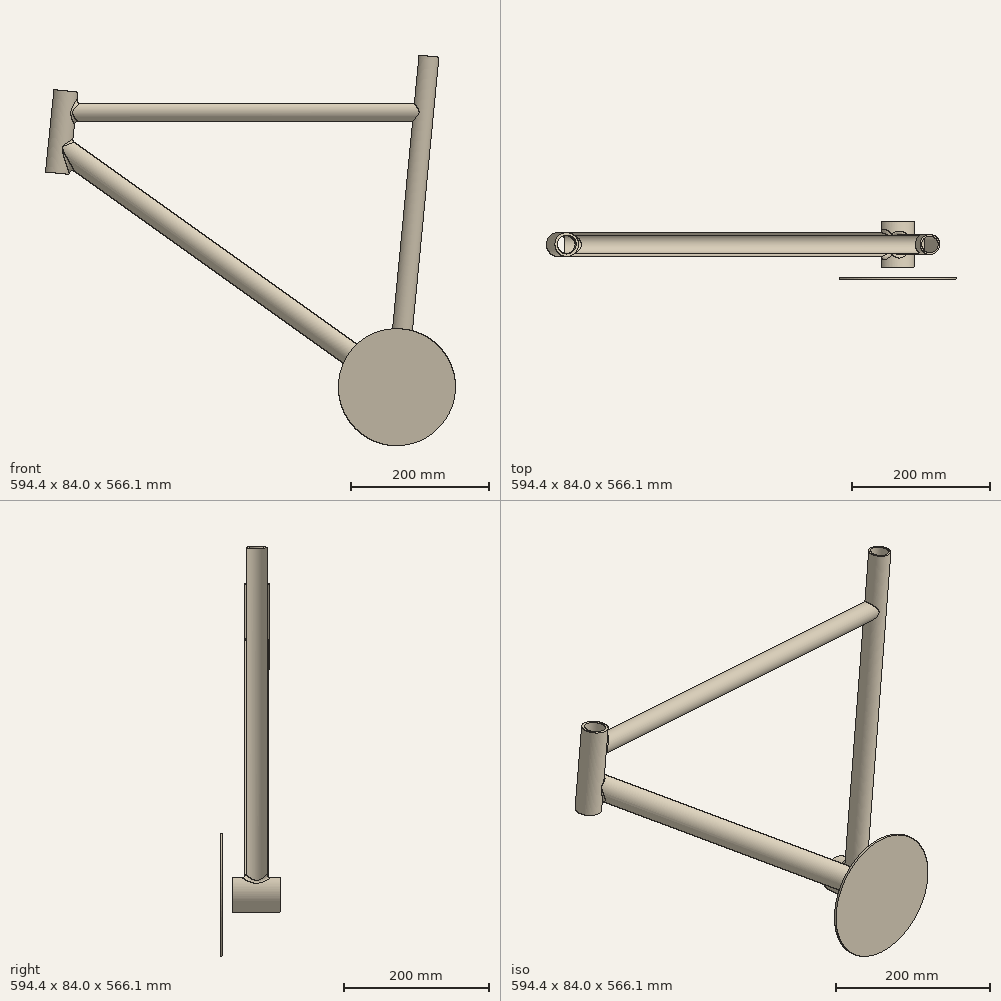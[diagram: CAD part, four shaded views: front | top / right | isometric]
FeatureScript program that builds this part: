
annotation { "Feature Type Name" : "Feature", "Feature Type Description" : "" }
export const myFeature = defineFeature(function(context is Context, id is Id, definition is map)
    precondition{}
    {
        {
            var Q0;
            Q0=qCreatedBy(makeId("Front.planeOp"),FACE);
            var sketch = newSketch(context, id + "F0", { "sketchPlane" : qUnion([Q0])});
            skLineSegment(sketch, "E0", {"start": v(0, 0) * mm, "end": v(-488.26, 348.72) * mm});
            skLineSegment(sketch, "E1", {"start": v(0, 0) * mm, "end": v(46.5, 479.84) * mm});
            skLineSegment(sketch, "E2", {"start": v(-483.17, 398.14) * mm, "end": v(38.58, 398.14) * mm});
            skCircle(sketch, "E3", {"center": v(0, 0) * mm, "radius": 24.13 * mm});
            skLineSegment(sketch, "E4", {"start": v(38.58, 398.14) * mm, "end": v(398.64, 35.69) * mm});
            skLineSegment(sketch, "E5", {"start": v(398.64, 35.69) * mm, "end": v(0, 0) * mm});
            skCircle(sketch, "E6", {"center": v(398.64, 35.69) * mm, "radius": 330.2 * mm, "construction": true});
            skLineSegment(sketch, "E7", {"start": v(-483.17, 398.14) * mm, "end": v(-488.26, 348.72) * mm});
            skLineSegment(sketch, "E8", {"start": v(-483.17, 398.14) * mm, "end": v(-483.17, 489.5) * mm, "construction": true});
            skSolve(sketch);
        }
        {
            var Q0;
            {var subQ1=sQuery(id+"F0.wireOp",EDGE,"E0");var subQ3=sQuery(id+"F0.wireOp",EDGE,"E3");var subQ4=makeQuery(id+"F0.imprint","INTERSECT",VERTEX,{"derivedFrom":[subQ1,subQ3]});Q0=makeQuery(id+"F0.imprint","IMPRINT",FACE,{"disambiguationData":[TD([[makeQuery(id+"F0.imprint","IMPRINT",EDGE,{"disambiguationData":[TD([[subQ4,1.0]])],"derivedFrom":subQ3}),1.0]])]});}
            var Q1;
            {var subQ0=sQuery(id+"F0.wireOp",EDGE,"E5");var subQ3=sQuery(id+"F0.wireOp",EDGE,"E3");var subQ5=makeQuery(id+"F0.imprint","INTERSECT",VERTEX,{"derivedFrom":[subQ3,subQ0]});Q1=makeQuery(id+"F0.imprint","IMPRINT",FACE,{"disambiguationData":[TD([[makeQuery(id+"F0.imprint","IMPRINT",EDGE,{"disambiguationData":[TD([[subQ5,-1.0]])],"derivedFrom":subQ3}),1.0]])]});}
            var Q2;
            {var subQ1=sQuery(id+"F0.wireOp",EDGE,"E0");var subQ3=sQuery(id+"F0.wireOp",EDGE,"E3");var subQ4=makeQuery(id+"F0.imprint","INTERSECT",VERTEX,{"derivedFrom":[subQ1,subQ3]});Q2=makeQuery(id+"F0.imprint","IMPRINT",FACE,{"disambiguationData":[TD([[makeQuery(id+"F0.imprint","IMPRINT",EDGE,{"disambiguationData":[TD([[subQ4,-1.0]])],"derivedFrom":subQ3}),1.0]])]});}
            var Q3;
            Q3=sQuery(id+"F0.wireOp",EDGE,"E3");
            extrude(context, id + "F1", {"entities" : qUnion([Q0, Q1, Q2]), "surfaceEntities" : qUnion([Q3]), "endBound" : BoundingType.SYMMETRIC, "depth" : 67 * mm, "offsetDistance" : 25 * mm});
        }
        {
            var Q0;
            Q0=qCreatedBy(makeId("Front.planeOp"),FACE);
            var sketch = newSketch(context, id + "F2", { "sketchPlane" : qUnion([Q0])});
            skLineSegment(sketch, "E9.0", {"start": v(0, 0) * mm, "end": v(46.5, 479.84) * mm, "construction": true});
            skCircle(sketch, "E10.0", {"center": v(0, 0) * mm, "radius": 24.13 * mm});
            skLineSegment(sketch, "E11", {"start": v(0, 0) * mm, "end": v(-14.43, 1.4) * mm});
            skLineSegment(sketch, "E12", {"start": v(-14.43, 1.4) * mm, "end": v(32.06, 481.24) * mm});
            skLineSegment(sketch, "E13", {"start": v(32.06, 481.24) * mm, "end": v(46.5, 479.84) * mm});
            skLineSegment(sketch, "E14", {"start": v(34.54, 481) * mm, "end": v(-11.95, 1.16) * mm});
            skSolve(sketch);
        }
        {
            var Q0;
            {var subQ0=sQuery(id+"F2.wireOp",EDGE,"E13");Q0=makeQuery(id+"F2.imprint","IMPRINT",FACE,{"disambiguationData":[TD([[makeQuery(id+"F2.imprint","IMPRINT",EDGE,{"derivedFrom":subQ0}),-1.0]])]});}
            var Q1;
            Q1=sQuery(id+"F2.wireOp",EDGE,"E9.0");
            revolve(context, id + "F3", {"surfaceOperationType" : NewSurfaceOperationType.NEW, "entities" : qUnion([Q0]), "axis" : qUnion([Q1]), "revolveType" : RevolveType.FULL});
        }
        {
            var Q0;
            Q0=qCreatedBy(makeId("Front.planeOp"),FACE);
            var sketch = newSketch(context, id + "F4", { "sketchPlane" : qUnion([Q0])});
            skLineSegment(sketch, "E15", {"start": v(-479.93, 429.59) * mm, "end": v(-462.64, 427.8) * mm});
            skLineSegment(sketch, "E16", {"start": v(-462.64, 427.8) * mm, "end": v(-474.94, 308.44) * mm});
            skLineSegment(sketch, "E17", {"start": v(-474.94, 308.44) * mm, "end": v(-492.23, 310.22) * mm});
            skLineSegment(sketch, "E18", {"start": v(-466.36, 428.19) * mm, "end": v(-478.66, 308.82) * mm});
            skLineSegment(sketch, "E19.0", {"start": v(-479.93, 429.59) * mm, "end": v(-492.23, 310.22) * mm, "construction": true});
            skPoint(sketch, "E20.orphan", {"position": v(-483.17, 398.14) * mm});
            skPoint(sketch, "E21.orphan", {"position": v(-488.26, 348.72) * mm});
            skSolve(sketch);
        }
        {
            var Q0;
            Q0 = qSketchRegion(id + "F4", true);
            var Q1;
            Q1=sQuery(id+"F0.wireOp",EDGE,"E7");
            revolve(context, id + "F5", {"surfaceOperationType" : NewSurfaceOperationType.NEW, "entities" : qUnion([Q0]), "axis" : qUnion([Q1]), "revolveType" : RevolveType.FULL});
        }
        {
            var Q0;
            Q0=qCreatedBy(makeId("Front.planeOp"),FACE);
            var sketch = newSketch(context, id + "F6", { "sketchPlane" : qUnion([Q0])});
            skLineSegment(sketch, "E22.0", {"start": v(-483.17, 398.14) * mm, "end": v(38.58, 398.14) * mm, "construction": true});
            skLineSegment(sketch, "E23", {"start": v(-483.17, 398.14) * mm, "end": v(-483.17, 385.14) * mm});
            skLineSegment(sketch, "E24", {"start": v(-483.17, 385.14) * mm, "end": v(38.58, 385.14) * mm});
            skLineSegment(sketch, "E25", {"start": v(38.58, 385.14) * mm, "end": v(38.58, 398.14) * mm});
            skLineSegment(sketch, "E26", {"start": v(-483.17, 386.14) * mm, "end": v(38.58, 386.14) * mm});
            skSolve(sketch);
        }
        {
            var Q0;
            Q0 = qSketchRegion(id + "F6", true);
            var Q1;
            Q1=sQuery(id+"F0.wireOp",EDGE,"E2");
            revolve(context, id + "F7", {"surfaceOperationType" : NewSurfaceOperationType.NEW, "entities" : qUnion([Q0]), "axis" : qUnion([Q1]), "revolveType" : RevolveType.FULL});
        }
        {
            var Q0;
            Q0=qCreatedBy(makeId("Front.planeOp"),FACE);
            var sketch = newSketch(context, id + "F8", { "sketchPlane" : qUnion([Q0])});
            skLineSegment(sketch, "E27.0", {"start": v(0, 0) * mm, "end": v(-488.26, 348.72) * mm, "construction": true});
            skLineSegment(sketch, "E28", {"start": v(-488.26, 348.72) * mm, "end": v(-498.14, 334.88) * mm});
            skLineSegment(sketch, "E29", {"start": v(-498.14, 334.88) * mm, "end": v(-9.88, -13.83) * mm});
            skLineSegment(sketch, "E30", {"start": v(-9.88, -13.83) * mm, "end": v(0, 0) * mm});
            skLineSegment(sketch, "E31", {"start": v(-497.56, 335.7) * mm, "end": v(-9.3, -13.02) * mm});
            skSolve(sketch);
        }
        {
            var Q0;
            Q0 = qSketchRegion(id + "F8", true);
            var Q1;
            Q1=sQuery(id+"F8.wireOp",EDGE,"E27.0");
            revolve(context, id + "F9", {"surfaceOperationType" : NewSurfaceOperationType.NEW, "entities" : qUnion([Q0]), "axis" : qUnion([Q1]), "revolveType" : RevolveType.FULL});
        }
        {
            var Q0;
            Q0=makeQuery(id+"F5.opRevolve","SWEPT_BODY",BODY,{"disambiguationData":[OSD([sQuery(id+"F4.wireOp",EDGE,"E15"),sQuery(id+"F4.wireOp",EDGE,"E16"),sQuery(id+"F4.wireOp",EDGE,"E17"),sQuery(id+"F4.wireOp",EDGE,"E18")])]});
            var Q1;
            Q1=makeQuery(id+"F3.opRevolve","SWEPT_BODY",BODY,{"disambiguationData":[OSD([sQuery(id+"F2.wireOp",EDGE,"E10.0"),sQuery(id+"F2.wireOp",EDGE,"E12"),sQuery(id+"F2.wireOp",EDGE,"E13"),sQuery(id+"F2.wireOp",EDGE,"E14")])]});
            var Q2;
            Q2=makeQuery(id+"F7.opRevolve","SWEPT_BODY",BODY,{"disambiguationData":[OSD([sQuery(id+"F6.wireOp",EDGE,"E23"),sQuery(id+"F6.wireOp",EDGE,"E24"),sQuery(id+"F6.wireOp",EDGE,"E25"),sQuery(id+"F6.wireOp",EDGE,"E26")])]});
            var Q3;
            Q3=makeQuery(id+"F9.opRevolve","SWEPT_BODY",BODY,{"disambiguationData":[OSD([sQuery(id+"F8.wireOp",EDGE,"E28"),sQuery(id+"F8.wireOp",EDGE,"E29"),sQuery(id+"F8.wireOp",EDGE,"E30"),sQuery(id+"F8.wireOp",EDGE,"E31")])]});
            booleanBodies(context, id + "F10", {"operationType" : BooleanOperationType.SUBTRACTION, "tools" : qUnion([Q0, Q1]), "targets" : qUnion([Q2, Q3]), "keepTools" : true});
        }
        {
            var Q0;
            Q0=makeQuery(id+"F1.opExtrude","SWEPT_BODY",BODY,{"disambiguationData":[OSD([sQuery(id+"F0.wireOp",EDGE,"E3")])]});
            var Q1;
            Q1=makeQuery(id+"F10.opBoolean","SPLIT",BODY,{"disambiguationData":[OD(0.0)],"derivedFrom":makeQuery(id+"F9.opRevolve","SWEPT_BODY",BODY,{"disambiguationData":[OSD([sQuery(id+"F8.wireOp",EDGE,"E28"),sQuery(id+"F8.wireOp",EDGE,"E29"),sQuery(id+"F8.wireOp",EDGE,"E30"),sQuery(id+"F8.wireOp",EDGE,"E31")])]})});
            var Q2;
            Q2=makeQuery(id+"F3.opRevolve","SWEPT_BODY",BODY,{"disambiguationData":[OSD([sQuery(id+"F2.wireOp",EDGE,"E10.0"),sQuery(id+"F2.wireOp",EDGE,"E12"),sQuery(id+"F2.wireOp",EDGE,"E13"),sQuery(id+"F2.wireOp",EDGE,"E14")])]});
            booleanBodies(context, id + "F11", {"operationType" : BooleanOperationType.SUBTRACTION, "tools" : qUnion([Q0]), "targets" : qUnion([Q1, Q2]), "keepTools" : true});
        }
        {
            var Q0;
            Q0=makeQuery(id+"F5.opRevolve","SWEPT_BODY",BODY,{"disambiguationData":[OSD([sQuery(id+"F4.wireOp",EDGE,"E15"),sQuery(id+"F4.wireOp",EDGE,"E16"),sQuery(id+"F4.wireOp",EDGE,"E17"),sQuery(id+"F4.wireOp",EDGE,"E18")])]});
            var Q1;
            Q1=makeQuery(id+"F10.opBoolean","SPLIT",BODY,{"disambiguationData":[OD(1.0)],"derivedFrom":makeQuery(id+"F7.opRevolve","SWEPT_BODY",BODY,{"disambiguationData":[OSD([sQuery(id+"F6.wireOp",EDGE,"E23"),sQuery(id+"F6.wireOp",EDGE,"E24"),sQuery(id+"F6.wireOp",EDGE,"E25"),sQuery(id+"F6.wireOp",EDGE,"E26")])]})});
            var Q2;
            Q2=makeQuery(id+"F3.opRevolve","SWEPT_BODY",BODY,{"disambiguationData":[OSD([sQuery(id+"F2.wireOp",EDGE,"E10.0"),sQuery(id+"F2.wireOp",EDGE,"E12"),sQuery(id+"F2.wireOp",EDGE,"E13"),sQuery(id+"F2.wireOp",EDGE,"E14")])]});
            var Q3;
            Q3=makeQuery(id+"F11.opBoolean","SPLIT",BODY,{"disambiguationData":[OD(0.0)],"derivedFrom":makeQuery(id+"F10.opBoolean","SPLIT",BODY,{"disambiguationData":[OD(0.0)],"derivedFrom":makeQuery(id+"F9.opRevolve","SWEPT_BODY",BODY,{"disambiguationData":[OSD([sQuery(id+"F8.wireOp",EDGE,"E28"),sQuery(id+"F8.wireOp",EDGE,"E29"),sQuery(id+"F8.wireOp",EDGE,"E30"),sQuery(id+"F8.wireOp",EDGE,"E31")])]})})});
            var Q4;
            Q4=makeQuery(id+"F1.opExtrude","SWEPT_BODY",BODY,{"disambiguationData":[OSD([sQuery(id+"F0.wireOp",EDGE,"E3")])]});
            booleanBodies(context, id + "F12", {"operationType" : BooleanOperationType.UNION, "tools" : qUnion([Q0, Q1, Q2, Q3, Q4]), "keepTools" : true});
        }
        {
            var Q0;
            Q0=makeQuery(id+"F10.opBoolean","INTERSECT",EDGE,{"derivedFrom":[makeQuery(id+"F5.opRevolve","SWEPT_FACE",FACE,{"disambiguationData":[OSD([sQuery(id+"F4.wireOp",EDGE,"E16")])]}),makeQuery(id+"F9.opRevolve","SWEPT_FACE",FACE,{"disambiguationData":[OSD([sQuery(id+"F8.wireOp",EDGE,"E29")])]})]});
            var Q1;
            Q1=makeQuery(id+"F10.opBoolean","INTERSECT",EDGE,{"derivedFrom":[makeQuery(id+"F5.opRevolve","SWEPT_FACE",FACE,{"disambiguationData":[OSD([sQuery(id+"F4.wireOp",EDGE,"E16")])]}),makeQuery(id+"F7.opRevolve","SWEPT_FACE",FACE,{"disambiguationData":[OSD([sQuery(id+"F6.wireOp",EDGE,"E24")])]})]});
            var Q2;
            {var subQ0=makeQuery(id+"F1.opExtrude","SWEPT_FACE",FACE,{"disambiguationData":[OSD([sQuery(id+"F0.wireOp",EDGE,"E3")])]});var subQ1=makeQuery(id+"F3.opRevolve","SWEPT_FACE",FACE,{"disambiguationData":[OSD([sQuery(id+"F2.wireOp",EDGE,"E12")])]});Q2=makeQuery(id+"F12.opBoolean","SPLIT",EDGE,{"disambiguationData":[TD([makeQuery(id+"F9.opRevolve","SWEPT_FACE",FACE,{"disambiguationData":[OSD([sQuery(id+"F8.wireOp",EDGE,"E29")])]})])],"derivedFrom":makeQuery(id+"F11.opBoolean","INTERSECT",EDGE,{"derivedFrom":[subQ0,subQ1]})});}
            var Q3;
            Q3=makeQuery(id+"F11.opBoolean","INTERSECT",EDGE,{"disambiguationData":[OD(0.0)],"derivedFrom":[makeQuery(id+"F1.opExtrude","SWEPT_FACE",FACE,{"disambiguationData":[OSD([sQuery(id+"F0.wireOp",EDGE,"E3")])]}),makeQuery(id+"F10.opBoolean","SPLIT",FACE,{"disambiguationData":[TD([makeQuery(id+"F3.opRevolve","SWEPT_FACE",FACE,{"disambiguationData":[OSD([sQuery(id+"F2.wireOp",EDGE,"E10.0")])]}),makeQuery(id+"F3.opRevolve","SWEPT_FACE",FACE,{"disambiguationData":[OSD([sQuery(id+"F2.wireOp",EDGE,"E12")])]}),makeQuery(id+"F3.opRevolve","SWEPT_FACE",FACE,{"disambiguationData":[OSD([sQuery(id+"F2.wireOp",EDGE,"E14")])]}),makeQuery(id+"F5.opRevolve","SWEPT_FACE",FACE,{"disambiguationData":[OSD([sQuery(id+"F4.wireOp",EDGE,"E16")])]}),makeQuery(id+"F9.opRevolve","SWEPT_FACE",FACE,{"disambiguationData":[OSD([sQuery(id+"F8.wireOp",EDGE,"E30")])]})])],"derivedFrom":makeQuery(id+"F9.opRevolve","SWEPT_FACE",FACE,{"disambiguationData":[OSD([sQuery(id+"F8.wireOp",EDGE,"E29")])]})})]});
            var Q4;
            Q4=makeQuery(id+"F10.opBoolean","INTERSECT",EDGE,{"derivedFrom":[makeQuery(id+"F3.opRevolve","SWEPT_FACE",FACE,{"disambiguationData":[OSD([sQuery(id+"F2.wireOp",EDGE,"E12")])]}),makeQuery(id+"F7.opRevolve","SWEPT_FACE",FACE,{"disambiguationData":[OSD([sQuery(id+"F6.wireOp",EDGE,"E24")])]})]});
            fillet(context, id + "F13", {"entities" : qUnion([Q0, Q1, Q2, Q3, Q4]), "radius" : 5 * mm, "allowEdgeOverflow" : false});
        }
        {
            var Q0;
            Q0=makeQuery(id+"F10.opBoolean","SPLIT",BODY,{"disambiguationData":[OD(2.0)],"derivedFrom":makeQuery(id+"F9.opRevolve","SWEPT_BODY",BODY,{"disambiguationData":[OSD([sQuery(id+"F8.wireOp",EDGE,"E28"),sQuery(id+"F8.wireOp",EDGE,"E29"),sQuery(id+"F8.wireOp",EDGE,"E30"),sQuery(id+"F8.wireOp",EDGE,"E31")])]})});
            var Q1;
            Q1=makeQuery(id+"F10.opBoolean","SPLIT",BODY,{"disambiguationData":[OD(3.0)],"derivedFrom":makeQuery(id+"F7.opRevolve","SWEPT_BODY",BODY,{"disambiguationData":[OSD([sQuery(id+"F6.wireOp",EDGE,"E23"),sQuery(id+"F6.wireOp",EDGE,"E24"),sQuery(id+"F6.wireOp",EDGE,"E25"),sQuery(id+"F6.wireOp",EDGE,"E26")])]})});
            var Q2;
            Q2=makeQuery(id+"F10.opBoolean","SPLIT",BODY,{"disambiguationData":[OD(1.0)],"derivedFrom":makeQuery(id+"F9.opRevolve","SWEPT_BODY",BODY,{"disambiguationData":[OSD([sQuery(id+"F8.wireOp",EDGE,"E28"),sQuery(id+"F8.wireOp",EDGE,"E29"),sQuery(id+"F8.wireOp",EDGE,"E30"),sQuery(id+"F8.wireOp",EDGE,"E31")])]})});
            var Q3;
            Q3=makeQuery(id+"F10.opBoolean","SPLIT",BODY,{"disambiguationData":[OD(4.0)],"derivedFrom":makeQuery(id+"F7.opRevolve","SWEPT_BODY",BODY,{"disambiguationData":[OSD([sQuery(id+"F6.wireOp",EDGE,"E23"),sQuery(id+"F6.wireOp",EDGE,"E24"),sQuery(id+"F6.wireOp",EDGE,"E25"),sQuery(id+"F6.wireOp",EDGE,"E26")])]})});
            var Q4;
            Q4=makeQuery(id+"F10.opBoolean","SPLIT",BODY,{"disambiguationData":[OD(2.0)],"derivedFrom":makeQuery(id+"F7.opRevolve","SWEPT_BODY",BODY,{"disambiguationData":[OSD([sQuery(id+"F6.wireOp",EDGE,"E23"),sQuery(id+"F6.wireOp",EDGE,"E24"),sQuery(id+"F6.wireOp",EDGE,"E25"),sQuery(id+"F6.wireOp",EDGE,"E26")])]})});
            var Q5;
            Q5=makeQuery(id+"F10.opBoolean","SPLIT",BODY,{"disambiguationData":[OD(1.0)],"derivedFrom":makeQuery(id+"F7.opRevolve","SWEPT_BODY",BODY,{"disambiguationData":[OSD([sQuery(id+"F6.wireOp",EDGE,"E23"),sQuery(id+"F6.wireOp",EDGE,"E24"),sQuery(id+"F6.wireOp",EDGE,"E25"),sQuery(id+"F6.wireOp",EDGE,"E26")])]})});
            var Q6;
            Q6=makeQuery(id+"F11.opBoolean","SPLIT",BODY,{"disambiguationData":[OD(1.0)],"derivedFrom":makeQuery(id+"F10.opBoolean","SPLIT",BODY,{"disambiguationData":[OD(0.0)],"derivedFrom":makeQuery(id+"F9.opRevolve","SWEPT_BODY",BODY,{"disambiguationData":[OSD([sQuery(id+"F8.wireOp",EDGE,"E28"),sQuery(id+"F8.wireOp",EDGE,"E29"),sQuery(id+"F8.wireOp",EDGE,"E30"),sQuery(id+"F8.wireOp",EDGE,"E31")])]})})});
            deleteBodies(context, id + "F14", {"entities" : qUnion([Q0, Q1, Q2, Q3, Q4, Q5, Q6])});
        }
        {
            var Q0;
            Q0=makeQuery(id+"F1.opExtrude","CAP_FACE",FACE,{"disambiguationData":[OSD([sQuery(id+"F0.wireOp",EDGE,"E3")])],"isStart":false});
            cPlane(context, id + "F15", {"entities" : qUnion([Q0]), "cplaneType" : CPlaneType.OFFSET, "offset" : 14 * mm, "width" : 150 * mm, "height" : 150 * mm});
        }
        {
            var Q0;
            Q0=qCreatedBy(id+"F15.planeOp",FACE);
            var sketch = newSketch(context, id + "F16", { "sketchPlane" : qUnion([Q0])});
            skCircle(sketch, "E32", {"center": v(0, 0) * mm, "radius": 84.9 * mm});
            skSolve(sketch);
        }
        {
            var Q0;
            Q0 = qSketchRegion(id + "F16", true);
            extrude(context, id + "F17", {"entities" : qUnion([Q0]), "depth" : 3 * mm, "offsetDistance" : 25 * mm});
        }
    });
